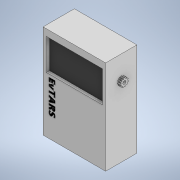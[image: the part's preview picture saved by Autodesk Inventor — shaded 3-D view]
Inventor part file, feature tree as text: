
AUTODESK INVENTOR PART (.ipt)
format: ipt  version: 2021 (Build 250183000, 183)  size: 409,600 bytes
history: native  units: mm
features: sketch x5, extrude x4, emboss x1
ambient origin geometry x8: Origin, YZ Plane, XZ Plane, XY Plane, X Axis, Y Axis, Z Axis, Center Point
bodies: Solid1 (feature_tree)
feature tree (10):
  extrude  "Extrusion1"  Depth=50.0mm
  extrude  "Extrusion2"  Depth=10.0mm
  extrude  "Extrusion3"  Depth=37.0mm
  emboss  "Emboss1"
  extrude  "Extrusion4"  Depth=0.5mm
  sketch  "Sketch1"  dims[d0=100.0mm d1=50.0mm]
  sketch  "Sketch2"  dims[d2=150.0mm d3=0.0mm d4=10.0mm]
  sketch  "Sketch3"  dims[d5=25.0mm d6=37.0mm]
  sketch  "Sketch4"  dims[d8=0.5mm d9=20.071286mm]
  sketch  "Sketch5"  dims[d10=6.5mm d11=110.0mm d13=360.0deg d15=5.0mm d16=5.0mm d17=0.0mm d19=110.0mm d20=25.0mm d21=37.0mm d22=0.5mm d23=20.071286mm d24=6.5mm d25=360.0deg d26=5.0mm d27=5.0mm d28=0.0mm d29=0.5mm d30=0.0mm d31=90.0mm d32=50.0mm d33=5.0mm d34=0.0mm]
